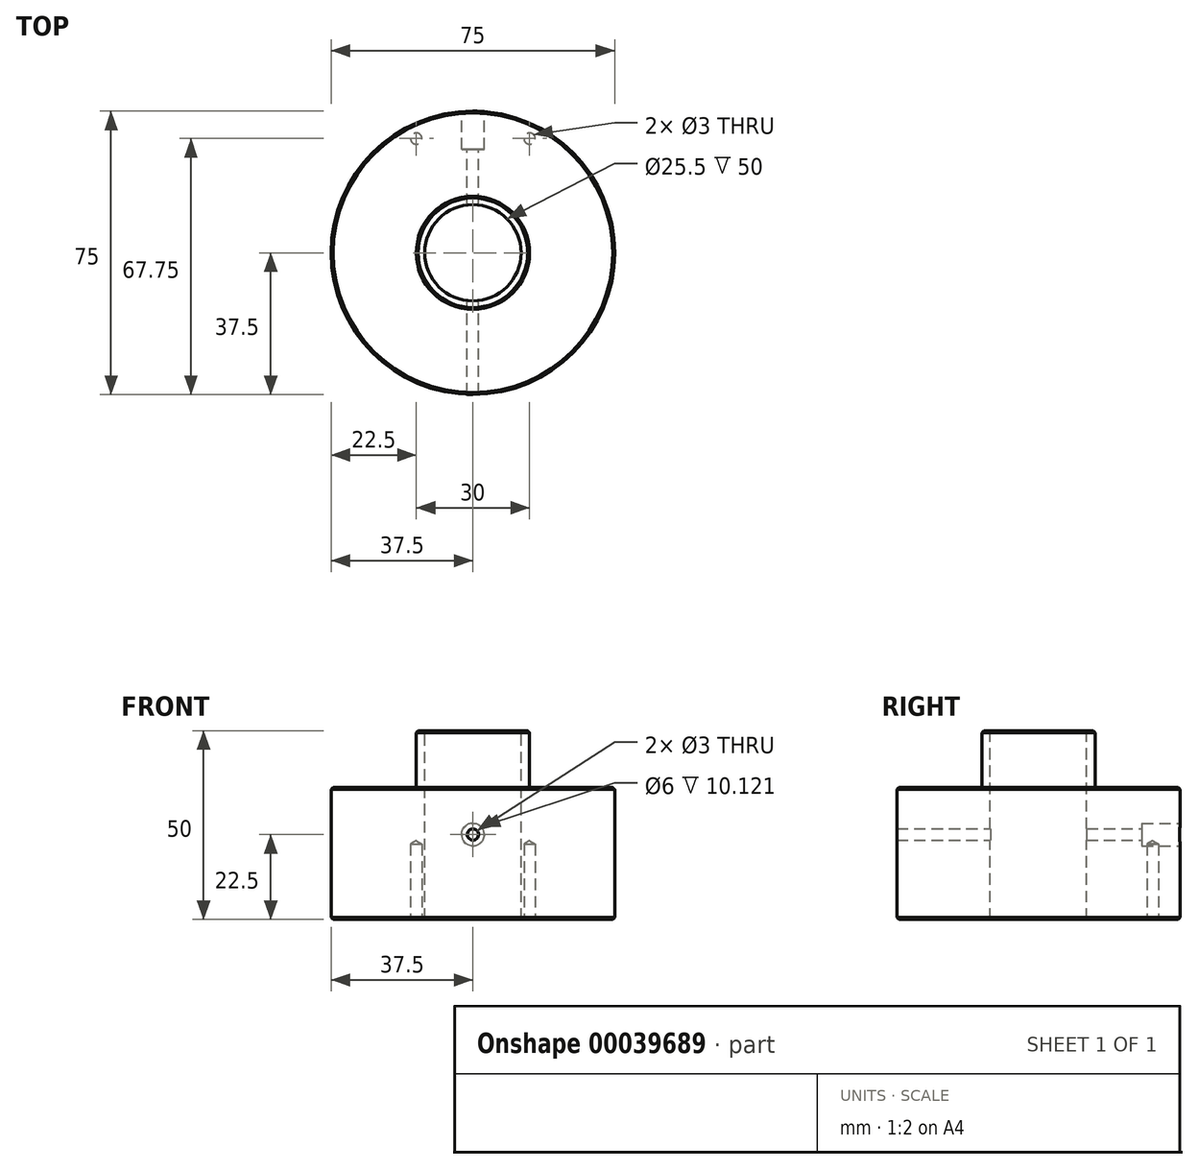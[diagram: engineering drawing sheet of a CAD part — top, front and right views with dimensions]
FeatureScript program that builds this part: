
annotation { "Feature Type Name" : "Feature", "Feature Type Description" : "" }
export const myFeature = defineFeature(function(context is Context, id is Id, definition is map)
    precondition{}
    {
        {
            var Q0;
            Q0=qCreatedBy(makeId("Top.planeOp"),FACE);
            var sketch = newSketch(context, id + "F0", { "sketchPlane" : qUnion([Q0])});
            skArc(sketch, "E0", {"start": v(30, 22.5) * mm, "mid": v(-37.5, 0) * mm, "end": v(30, -22.5) * mm});
            skArc(sketch, "E1", {"start": v(30, -22.5) * mm, "mid": v(37.5, 0) * mm, "end": v(30, 22.5) * mm});
            skSolve(sketch);
        }
        {
            var Q0;
            Q0=makeQuery(id+"F0.imprint","IMPRINT",FACE,{"disambiguationData":[TD([[makeQuery(id+"F0.imprint","IMPRINT",EDGE,{"derivedFrom":sQuery(id+"F0.wireOp",EDGE,"6c70eb9d-1247-4af5-9451-45589c62dc35")}),-1.0]])]});
            var Q1;
            Q1=makeQuery(id+"F0.imprint","IMPRINT",FACE,{"disambiguationData":[TD([[makeQuery(id+"F0.imprint","IMPRINT",EDGE,{"derivedFrom":sQuery(id+"F0.wireOp",EDGE,"E0")}),1.0]])]});
            extrude(context, id + "F1", {"entities" : qUnion([Q0, Q1]), "depth" : 25 * mm, "hasSecondDirection" : true, "secondDirectionOppositeDirection" : true, "secondDirectionDepth" : 10 * mm});
        }
        {
            var Q0;
            Q0=makeQuery(id+"F1.opExtrude","CAP_FACE",FACE,{"disambiguationData":[OSD([sQuery(id+"F0.wireOp",EDGE,"E0")])],"isStart":false});
            var sketch = newSketch(context, id + "F2", { "sketchPlane" : qUnion([Q0])});
            skCircle(sketch, "E2", {"center": v(0, 0) * mm, "radius": 15 * mm});
            skSolve(sketch);
        }
        {
            var Q0;
            Q0=makeQuery(id+"F2.imprint","IMPRINT",FACE,{"disambiguationData":[TD([[makeQuery(id+"F2.imprint","IMPRINT",EDGE,{"derivedFrom":sQuery(id+"F2.wireOp",EDGE,"E2")}),1.0]])]});
            extrude(context, id + "F3", {"entities" : qUnion([Q0]), "operationType" : NewBodyOperationType.ADD, "depth" : 15 * mm});
        }
        {
            var Q0;
            Q0=makeQuery(id+"F3.opExtrude","CAP_FACE",FACE,{"disambiguationData":[OSD([sQuery(id+"F2.wireOp",EDGE,"E2")])],"isStart":false});
            var sketch = newSketch(context, id + "F4", { "sketchPlane" : qUnion([Q0])});
            skCircle(sketch, "E3", {"center": v(0, 0) * mm, "radius": 12.75 * mm});
            skSolve(sketch);
        }
        {
            var Q0;
            Q0=makeQuery(id+"F4.imprint","IMPRINT",FACE,{"disambiguationData":[TD([[makeQuery(id+"F4.imprint","IMPRINT",EDGE,{"derivedFrom":sQuery(id+"F4.wireOp",EDGE,"E3")}),1.0]])]});
            extrude(context, id + "F5", {"entities" : qUnion([Q0]), "operationType" : NewBodyOperationType.REMOVE, "endBound" : BoundingType.UP_TO_NEXT, "oppositeDirection" : true, "depth" : 25 * mm});
        }
        {
            var Q0;
            Q0=qCreatedBy(makeId("Front.planeOp"),FACE);
            cPlane(context, id + "F6", {"entities" : qUnion([Q0]), "cplaneType" : CPlaneType.OFFSET, "offset" : 37.5 * mm, "oppositeDirection" : true, "width" : 150 * mm, "height" : 150 * mm});
        }
        {
            var Q0;
            Q0=qCreatedBy(id+"F6.planeOp",FACE);
            var sketch = newSketch(context, id + "F7", { "sketchPlane" : qUnion([Q0])});
            skPoint(sketch, "E4", {"position": v(0, 12.5) * mm});
            skSolve(sketch);
        }
        {
            var Q0;
            Q0=sQuery(id+"F7.wireOp",VERTEX,"E4");
            var Q1;
            Q1=makeQuery(id+"F1.opExtrude","SWEPT_BODY",BODY,{"disambiguationData":[OSD([sQuery(id+"F0.wireOp",EDGE,"E0"),sQuery(id+"F0.wireOp",EDGE,"7fe36a24-192a-45bf-846c-e6671ff0217e")])]});
            hole(context, id + "F8", {"style" : HoleStyle.C_BORE, "holeDiameter" : 3 * mm, "cBoreDiameter" : 6 * mm, "cBoreDepth" : 10 * mm, "endStyle" : HoleEndStyle.BLIND, "oppositeDirection" : true, "holeDepth" : 40 * mm, "locations" : qUnion([Q0]), "scope" : qUnion([Q1])});
        }
        {
            var Q0;
            Q0=makeQuery(id+"F1.opExtrude","CAP_FACE",FACE,{"disambiguationData":[OSD([sQuery(id+"F0.wireOp",EDGE,"E0"),sQuery(id+"F0.wireOp",EDGE,"E1")])],"isStart":true});
            var sketch = newSketch(context, id + "F9", { "sketchPlane" : qUnion([Q0])});
            skPoint(sketch, "E5", {"position": v(15, -30.25) * mm});
            skPoint(sketch, "E6.MirrorP", {"position": v(-15, -30.25) * mm});
            skSolve(sketch);
        }
        {
            var Q0;
            Q0=sQuery(id+"F9.wireOp",VERTEX,"E6.MirrorP");
            var Q1;
            Q1=sQuery(id+"F9.wireOp",VERTEX,"E5");
            var Q2;
            Q2=makeQuery(id+"F1.opExtrude","SWEPT_BODY",BODY,{"disambiguationData":[OSD([sQuery(id+"F0.wireOp",EDGE,"E0"),sQuery(id+"F0.wireOp",EDGE,"E1")])]});
            hole(context, id + "F10", {"style" : HoleStyle.SIMPLE, "holeDiameter" : 3 * mm, "endStyle" : HoleEndStyle.BLIND, "holeDepth" : 20 * mm, "locations" : qUnion([Q0, Q1]), "scope" : qUnion([Q2])});
        }
        {
            var Q0;
            Q0=qCreatedBy(makeId("Front.planeOp"),FACE);
            var sketch = newSketch(context, id + "F11", { "sketchPlane" : qUnion([Q0])});
            skPoint(sketch, "E7", {"position": v(0, 12.5) * mm});
            skSolve(sketch);
        }
        {
            var Q0;
            Q0=sQuery(id+"F11.wireOp",VERTEX,"E7");
            var Q1;
            Q1=makeQuery(id+"F1.opExtrude","SWEPT_BODY",BODY,{"disambiguationData":[OSD([sQuery(id+"F0.wireOp",EDGE,"E0"),sQuery(id+"F0.wireOp",EDGE,"E1")])]});
            hole(context, id + "F12", {"style" : HoleStyle.SIMPLE, "holeDiameter" : 3 * mm, "endStyle" : HoleEndStyle.THROUGH, "oppositeDirection" : true, "locations" : qUnion([Q0]), "scope" : qUnion([Q1])});
        }
        {
            var Q0;
            Q0=makeQuery(id+"F3.opExtrude","CAP_EDGE",EDGE,{"disambiguationData":[OSD([sQuery(id+"F2.wireOp",EDGE,"E2")])],"isStart":false});
            var Q1;
            Q1=makeQuery(id+"F5.boolean.opBoolean","COPY",EDGE,{"derivedFrom":makeQuery(id+"F5.opExtrude","CAP_EDGE",EDGE,{"disambiguationData":[OSD([sQuery(id+"F4.wireOp",EDGE,"E3")])],"isStart":true})});
            var Q2;
            Q2=makeQuery(id+"F1.opExtrude","CAP_EDGE",EDGE,{"disambiguationData":[OSD([sQuery(id+"F0.wireOp",EDGE,"E0"),sQuery(id+"F0.wireOp",EDGE,"E1")])],"isStart":false});
            var Q3;
            Q3=makeQuery(id+"F1.opExtrude","CAP_EDGE",EDGE,{"disambiguationData":[OSD([sQuery(id+"F0.wireOp",EDGE,"E0"),sQuery(id+"F0.wireOp",EDGE,"E1")])],"isStart":true});
            var Q4;
            Q4=makeQuery(id+"F5.boolean.opBoolean","COPY",EDGE,{"derivedFrom":makeQuery(id+"F5.opExtrude","TWEAK_EDGE",EDGE,{"derivedFrom":[makeQuery(id+"F1.opExtrude","CAP_FACE",FACE,{"disambiguationData":[OSD([sQuery(id+"F0.wireOp",EDGE,"E0"),sQuery(id+"F0.wireOp",EDGE,"E1")])],"isStart":true}),makeQuery(id+"F4.imprint","IMPRINT",EDGE,{"derivedFrom":sQuery(id+"F4.wireOp",EDGE,"E3")})]})});
            var Q5;
            Q5=makeQuery(id+"F3.opExtrude","CAP_EDGE",EDGE,{"disambiguationData":[OSD([sQuery(id+"F2.wireOp",EDGE,"E2")])],"isStart":true});
            chamfer(context, id + "F13", {"entities" : qUnion([Q0, Q1, Q2, Q3, Q4, Q5]), "width" : 0.5 * mm, "tangentPropagation" : true});
        }
    });
